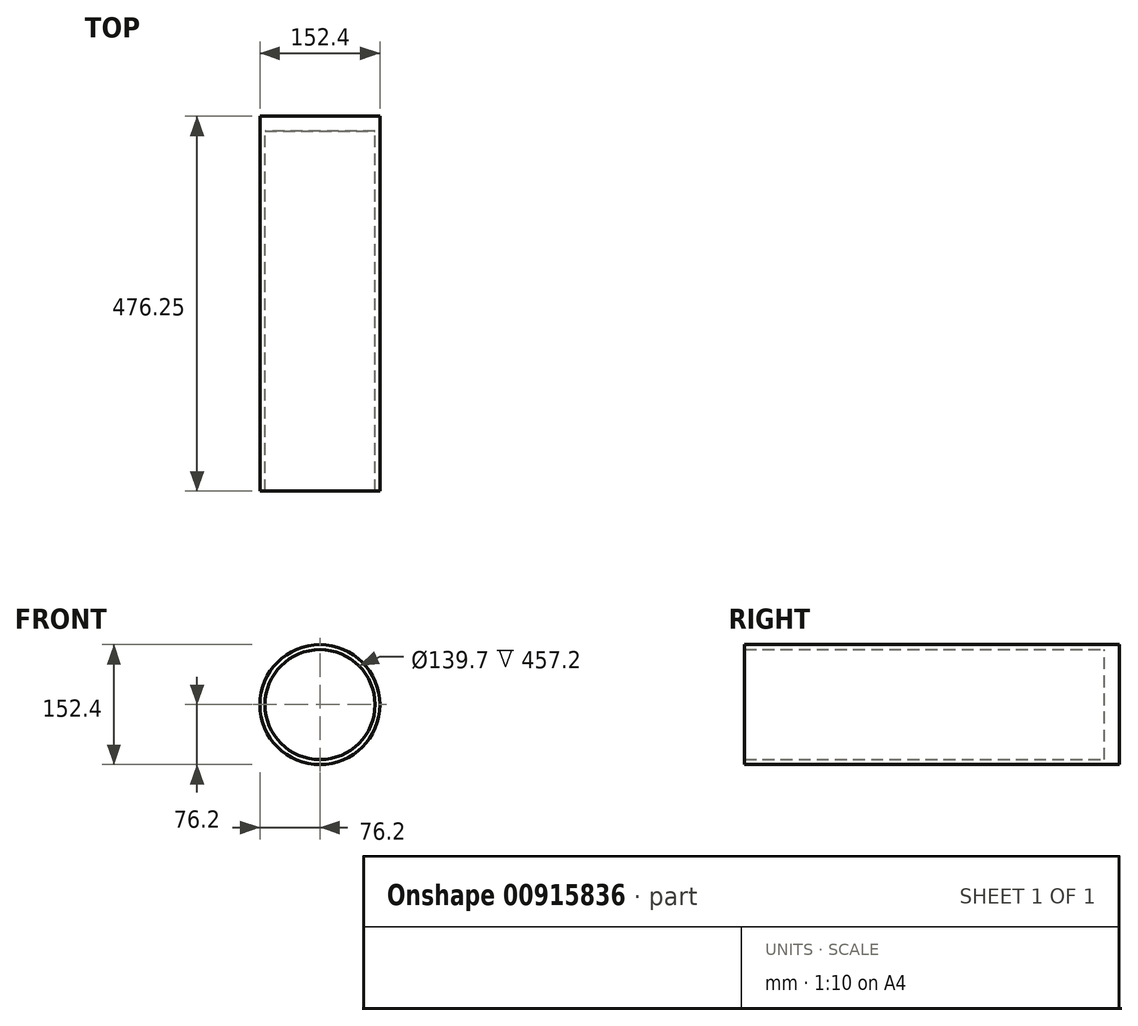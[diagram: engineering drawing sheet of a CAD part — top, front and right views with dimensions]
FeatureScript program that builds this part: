
annotation { "Feature Type Name" : "Feature", "Feature Type Description" : "" }
export const myFeature = defineFeature(function(context is Context, id is Id, definition is map)
    precondition{}
    {
        {
            var Q0;
            Q0=qCreatedBy(makeId("Front.planeOp"),FACE);
            var sketch = newSketch(context, id + "F0", { "sketchPlane" : qUnion([Q0])});
            skCircle(sketch, "E0", {"center": v(0, 0) * mm, "radius": 76.2 * mm});
            skCircle(sketch, "E1", {"center": v(0, 0) * mm, "radius": 69.85 * mm});
            skSolve(sketch);
        }
        {
            var Q0;
            Q0 = qSketchRegion(id + "F0", true);
            extrude(context, id + "F1", {"entities" : qUnion([Q0]), "depth" : 457.2 * mm, "offsetDistance" : 25.4 * mm});
        }
        {
            var Q0;
            Q0=makeQuery(id+"F1.opExtrude","CAP_FACE",FACE,{"disambiguationData":[OSD([sQuery(id+"F0.wireOp",EDGE,"E0"),sQuery(id+"F0.wireOp",EDGE,"E1")])],"isStart":true});
            var sketch = newSketch(context, id + "F2", { "sketchPlane" : qUnion([Q0])});
            skCircle(sketch, "E2", {"center": v(0, 0) * mm, "radius": 76.2 * mm});
            skSolve(sketch);
        }
        {
            var Q0;
            Q0 = qSketchRegion(id + "F2", true);
            extrude(context, id + "F3", {"entities" : qUnion([Q0]), "operationType" : NewBodyOperationType.ADD, "depth" : 19.05 * mm, "offsetDistance" : 25.4 * mm});
        }
    });
